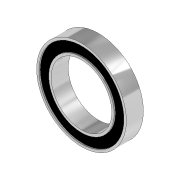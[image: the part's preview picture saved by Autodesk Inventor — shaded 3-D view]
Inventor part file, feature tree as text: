
AUTODESK INVENTOR PART (.ipt)
format: ipt  version: 2020 (Build 240168000, 168)  size: 124,928 bytes
history: native  units: in
note: dims shown in document units (in); Inventor stores cm internally (conversion verified against a paired STEP export)
features: extrude x3, sketch x3, projected_geometry x1
ambient origin geometry x8: Origin, YZ Plane, XZ Plane, XY Plane, X Axis, Y Axis, Z Axis, Center Point
bodies: Solid1 (feature_tree)
feature tree (7):
  extrude  "Extrusion1"  Depth=1.4567in
  extrude  "Extrusion2"  Depth=0.2756in
  extrude  "Extrusion3"  Depth=0.0197in TaperAngle=0.0deg
  sketch  "Sketch1"  dims[d0=0.9843in d1=1.4567in]
  sketch  "Sketch2"  dims[d2=0.2756in d3=0.0in d4=0.0394in]
  projected_geometry  "Projected Loop1"
  sketch  "Sketch3"  dims[d5=0.0394in d6=0.0197in d7=0.0in d8=0.0197in d9=0.0in]
